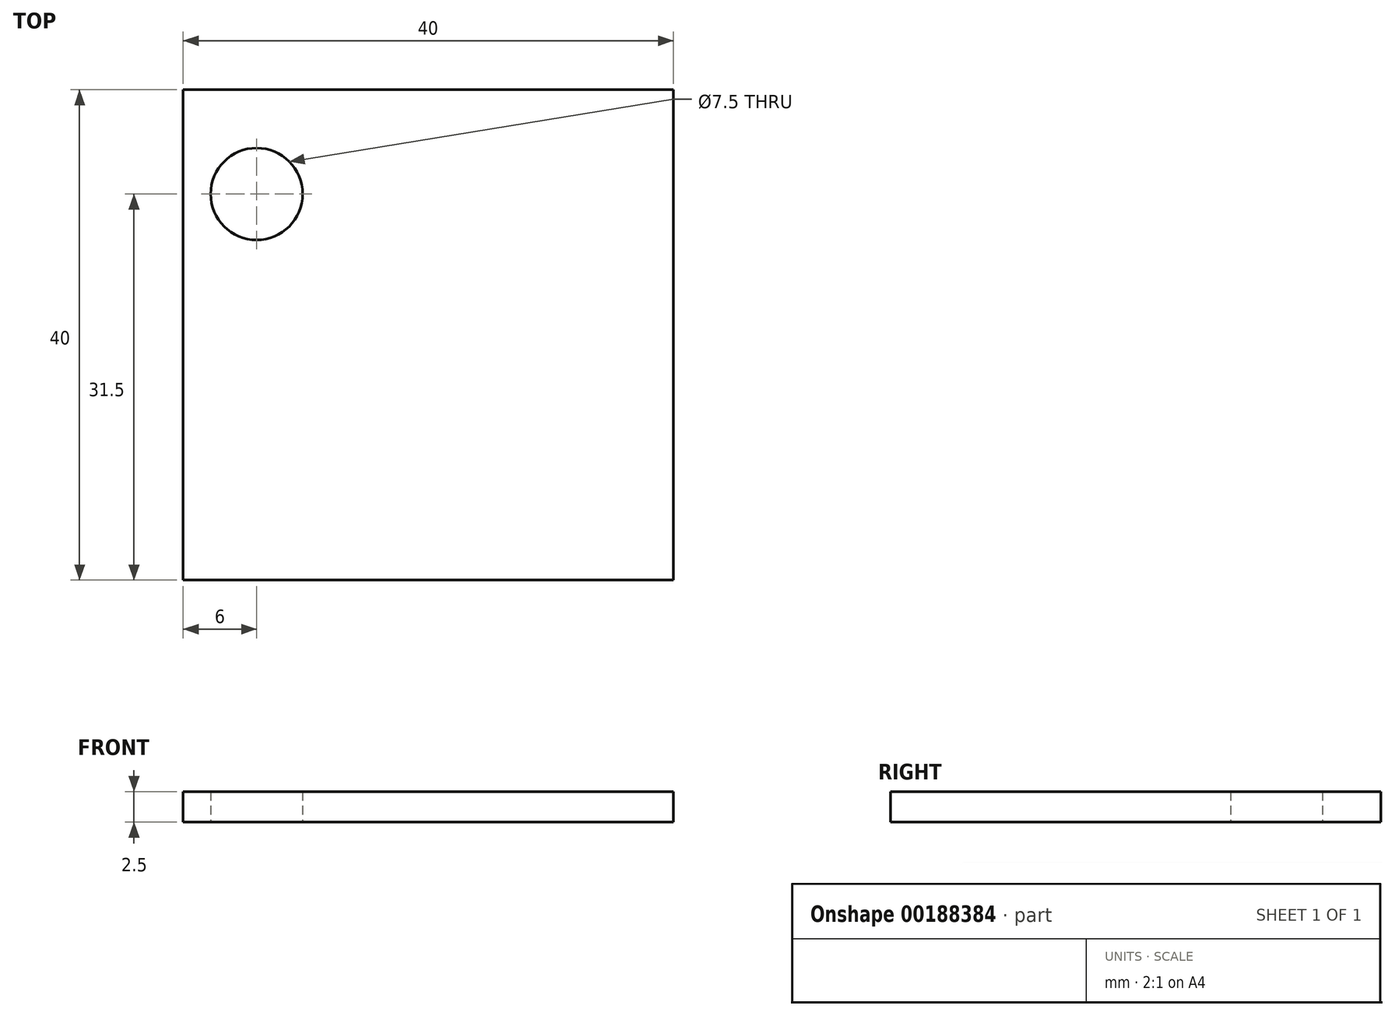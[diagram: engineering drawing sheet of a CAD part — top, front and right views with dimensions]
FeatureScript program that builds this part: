
annotation { "Feature Type Name" : "Feature", "Feature Type Description" : "" }
export const myFeature = defineFeature(function(context is Context, id is Id, definition is map)
    precondition{}
    {
        {
            var Q0;
            Q0=qCreatedBy(makeId("Top.planeOp"),FACE);
            var sketch = newSketch(context, id + "F0", { "sketchPlane" : qUnion([Q0])});
            skLineSegment(sketch, "E0.bottom", {"start": v(-40, 40) * mm, "end": v(0, 40) * mm});
            skLineSegment(sketch, "E0.top", {"start": v(-40, 0) * mm, "end": v(0, 0) * mm});
            skLineSegment(sketch, "E0.left", {"start": v(-40, 40) * mm, "end": v(-40, 0) * mm});
            skLineSegment(sketch, "E0.right", {"start": v(0, 40) * mm, "end": v(0, 0) * mm});
            skCircle(sketch, "E1", {"center": v(-34, 31.5) * mm, "radius": 3.75 * mm});
            skLineSegment(sketch, "E2", {"start": v(-34, 31.5) * mm, "end": v(-34, 40) * mm, "construction": true});
            skLineSegment(sketch, "E3", {"start": v(-34, 31.5) * mm, "end": v(-40, 31.5) * mm, "construction": true});
            skSolve(sketch);
        }
        {
            var Q0;
            Q0 = qSketchRegion(id + "F0", true);
            extrude(context, id + "F1", {"entities" : qUnion([Q0]), "depth" : 2.5 * mm});
        }
    });
